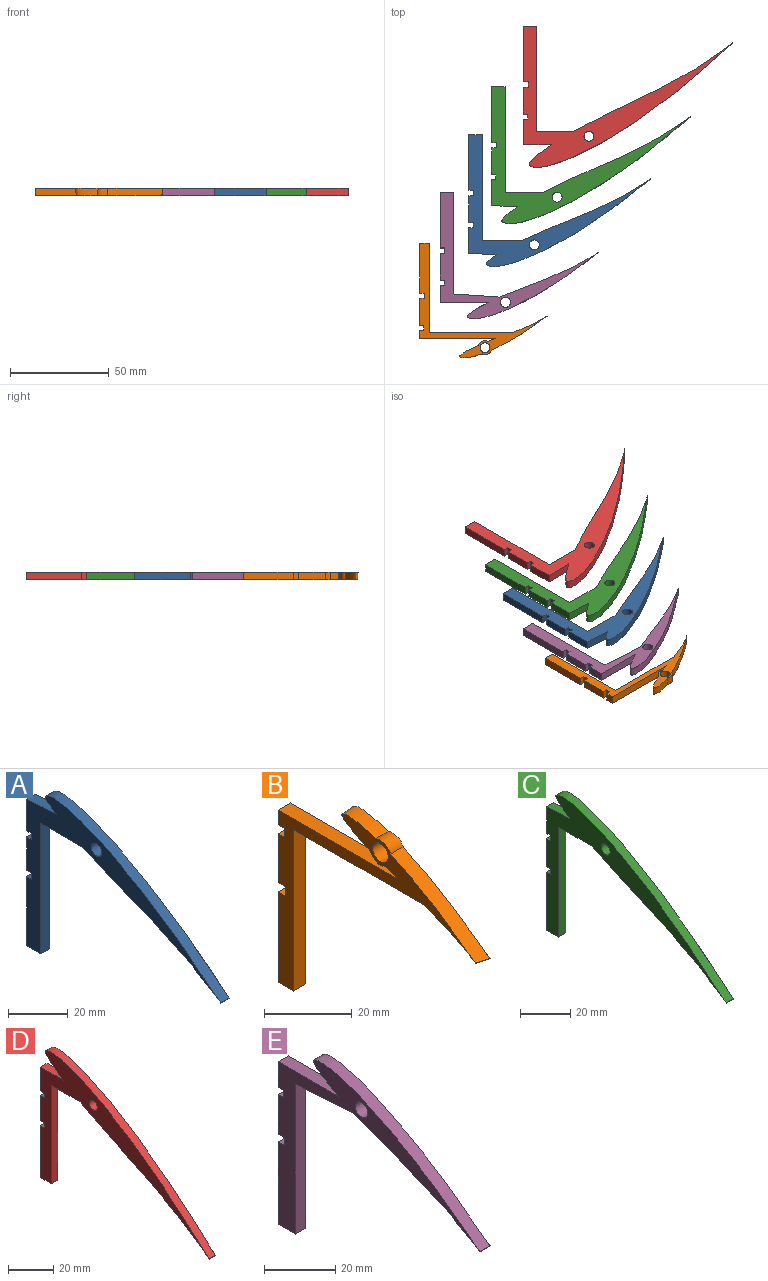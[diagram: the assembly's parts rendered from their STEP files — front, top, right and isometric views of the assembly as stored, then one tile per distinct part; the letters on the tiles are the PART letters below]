
ASSEMBLY  parts=5 mates=4
PART A: 19 faces, bbox 4x92x66.8 mm
  f0: plane 13.63x4mm, normal (0,1,0), area 54.5mm2, adj f2,f3,f13,f17
  f1: plane 28.27x4mm, normal (0,1,0), area 113.1mm2, adj f2,f3,f9,f12
  f2: plane 91.96x66.78mm, normal (-1,0,0), area 1042.6mm2, adj f0,f1,f4,f5,f6,f7,f8,f9
  f3: plane 91.96x66.78mm, normal (1,0,0), area 1042.6mm2, adj f0,f1,f4,f5,f6,f7,f8,f9
  f4: extruded ~81.29x43.68mm, area 702.9mm2, adj f2,f3,f5,f6
  f5: plane 4x0.96mm, normal (0,0,1), area 3.8mm2, adj f2,f3,f4,f7
  f6: plane 4x1.11mm, normal (0,-0.15,-0.99), area 4.5mm2, adj f2,f3,f4,f11
  f7: plane 13.06x4mm, normal (0,0.05,1), area 52.3mm2, adj f2,f3,f5,f8
  f8: plane 12.99x4mm, normal (0,1,0), area 51.9mm2, adj f2,f3,f7,f15
  f9: plane 6.75x4mm, normal (0,0,-1), area 27mm2, adj f1,f2,f3,f10
  f10: plane 53.49x4mm, normal (0,-1,0), area 214mm2, adj f2,f3,f9,f11
  f11: plane 18.8x4mm, normal (0,0,-1), area 75.2mm2, adj f2,f3,f6,f10
  f12: plane 4x2.41mm, normal (0,0,1), area 9.6mm2, adj f1,f2,f3,f14
  f13: plane 4x2.41mm, normal (0,0,-1), area 9.6mm2, adj f0,f2,f3,f14
  f14: plane 4x2.64mm, normal (0,1,0), area 10.5mm2, adj f2,f3,f12,f13
  f15: plane 4x2.18mm, normal (0,0,-1), area 8.7mm2, adj f2,f3,f8,f16
  f16: plane 4x2.52mm, normal (0,1,0), area 10.1mm2, adj f2,f3,f15,f17
  f17: plane 4x2.18mm, normal (0,0,1), area 8.7mm2, adj f0,f2,f3,f16
  f18: cylinder r=2.5mm len=5mm, axis (1,0,0), area 62.8mm2, adj f2,f3
PART B: 21 faces, bbox 61.1x65x59.3 mm
  f0: plane 13.63x4mm, normal (0,1,0), area 54.5mm2, adj f2,f3,f15,f19
  f1: plane 25.19x4mm, normal (0,1,0), area 100.8mm2, adj f2,f3,f13,f14
  f2: plane 65.03x58.52mm, normal (1,0,0), area 472.4mm2, adj f0,f1,f4,f5,f6,f7,f8,f9
  f3: plane 64.35x58.3mm, normal (-1,0,0), area 470.3mm2, adj f0,f1,f4,f5,f6,f7,f8,f9
  f4: bspline ~28.12x17.14mm, area 207.3mm2, adj f2,f3,f5,f10
  f5: cylinder r=3.5mm len=4.86mm, axis (-1,0,0), area 23.4mm2, adj f2,f3,f4,f8
  f6: cylinder r=3.5mm len=4.83mm, axis (-1,0,0), area 23.2mm2, adj f2,f3,f7,f8
  f7: bspline ~60.49x6.24mm, area 17.6mm2, adj f2,f3,f6,f11
  f8: bspline ~60.49x13.41mm, area 90.8mm2, adj f2,f3,f5,f6
  f9: plane 45.11x4mm, normal (0,-1,0), area 180.4mm2, adj f2,f3,f10,f13
  f10: plane 42.24x4.01mm, normal (0,0,-1), area 168.5mm2, adj f2,f3,f4,f9
  f11: plane 38.84x4.01mm, normal (0,0,1), area 155mm2, adj f2,f3,f7,f12
  f12: plane 4.08x4mm, normal (0,1,0), area 16.3mm2, adj f2,f3,f11,f17
  f13: plane 5.04x4mm, normal (0,0,-1), area 20.1mm2, adj f1,f2,f3,f9
  f14: plane 4x2.41mm, normal (0,0,1), area 9.6mm2, adj f1,f2,f3,f16
  f15: plane 4x2.41mm, normal (0,0,-1), area 9.6mm2, adj f0,f2,f3,f16
  f16: plane 4x2.64mm, normal (0,1,0), area 10.5mm2, adj f2,f3,f14,f15
  f17: plane 4x2.18mm, normal (0,0,-1), area 8.7mm2, adj f2,f3,f12,f18
  f18: plane 4x2.52mm, normal (0,1,0), area 10.1mm2, adj f2,f3,f17,f19
  f19: plane 4x2.18mm, normal (0,0,1), area 8.7mm2, adj f0,f2,f3,f18
  f20: cylinder r=2.5mm len=5mm, axis (1,0,0), area 62.8mm2, adj f2,f3
PART C: 17 faces, bbox 4x100.8x69.3 mm
  f0: plane 13.63x4mm, normal (0,1,0), area 54.5mm2, adj f2,f3,f11,f15
  f1: plane 28.27x4mm, normal (0,1,0), area 113.1mm2, adj f2,f3,f8,f10
  f2: plane 100.76x69.26mm, normal (-1,0,0), area 1079.5mm2, adj f0,f1,f4,f5,f6,f7,f8,f9
  f3: plane 100.76x69.26mm, normal (1,0,0), area 1079.5mm2, adj f0,f1,f4,f5,f6,f7,f8,f9
  f4: extruded ~93.53x53.84mm, area 829.8mm2, adj f2,f3,f5,f6
  f5: plane 18.8x4mm, normal (0,0,-1), area 75.2mm2, adj f2,f3,f4,f9
  f6: plane 13.06x4mm, normal (0,0.05,1), area 52.3mm2, adj f2,f3,f4,f7
  f7: plane 12.99x4mm, normal (0,1,0), area 51.9mm2, adj f2,f3,f6,f13
  f8: plane 6.75x4mm, normal (0,0,-1), area 27mm2, adj f1,f2,f3,f9
  f9: plane 53.49x4mm, normal (0,-1,0), area 214mm2, adj f2,f3,f5,f8
  f10: plane 4x2.41mm, normal (0,0,1), area 9.6mm2, adj f1,f2,f3,f12
  f11: plane 4x2.41mm, normal (0,0,-1), area 9.6mm2, adj f0,f2,f3,f12
  f12: plane 4x2.64mm, normal (0,1,0), area 10.5mm2, adj f2,f3,f10,f11
  f13: plane 4x2.18mm, normal (0,0,-1), area 8.7mm2, adj f2,f3,f7,f14
  f14: plane 4x2.52mm, normal (0,1,0), area 10.1mm2, adj f2,f3,f13,f15
  f15: plane 4x2.18mm, normal (0,0,1), area 8.7mm2, adj f0,f2,f3,f14
  f16: cylinder r=2.5mm len=5mm, axis (1,0,0), area 62.8mm2, adj f2,f3
PART D: 18 faces, bbox 4x105.7x71.5 mm
  f0: plane 13.63x4mm, normal (0,1,0), area 54.5mm2, adj f2,f3,f12,f16
  f1: plane 28.27x4mm, normal (0,1,0), area 113.1mm2, adj f2,f3,f8,f11
  f2: plane 105.66x71.45mm, normal (-1,0,0), area 1024.1mm2, adj f0,f1,f4,f6,f7,f8,f9,f10
  f3: plane 105.66x71.45mm, normal (1,0,0), area 1023.1mm2, adj f0,f1,f4,f6,f7,f8,f9,f10
  f4: extruded ~101.67x62.04mm, area 923.7mm2, adj f2,f3,f5,f6
  f5: plane 4.01x0.01mm, normal (0,-0.64,0.77), area 0mm2, adj f4,f10
  f6: plane 14.14x4mm, normal (0,0,1), area 56.6mm2, adj f2,f3,f4,f7
  f7: plane 12.99x4mm, normal (0,1,0), area 51.9mm2, adj f2,f3,f6,f14
  f8: plane 6.75x4mm, normal (0,0,-1), area 27mm2, adj f1,f2,f3,f9
  f9: plane 53.49x4mm, normal (0,-1,0), area 214mm2, adj f2,f3,f8,f10
  f10: plane 18.12x4mm, normal (0,0,-1), area 72.5mm2, adj f2,f3,f5,f9
  f11: plane 4x2.41mm, normal (0,0,1), area 9.6mm2, adj f1,f2,f3,f13
  f12: plane 4x2.41mm, normal (0,0,-1), area 9.6mm2, adj f0,f2,f3,f13
  f13: plane 4x2.64mm, normal (0,1,0), area 10.5mm2, adj f2,f3,f11,f12
  f14: plane 4x2.18mm, normal (0,0,-1), area 8.7mm2, adj f2,f3,f7,f15
  f15: plane 4x2.52mm, normal (0,1,0), area 10.1mm2, adj f2,f3,f14,f16
  f16: plane 4x2.18mm, normal (0,0,1), area 8.7mm2, adj f0,f2,f3,f15
  f17: cylinder r=2.5mm len=5mm, axis (1,0,0), area 62.8mm2, adj f2,f3
PART E: 17 faces, bbox 4x80x64.1 mm
  f0: plane 13.63x4mm, normal (0,1,0), area 54.5mm2, adj f2,f3,f11,f15
  f1: plane 28.27x4mm, normal (0,1,0), area 113.1mm2, adj f2,f3,f8,f10
  f2: plane 80.02x64.08mm, normal (-1,0,0), area 692.2mm2, adj f0,f1,f4,f5,f6,f7,f8,f9
  f3: plane 80.02x64.08mm, normal (1,0,0), area 692.2mm2, adj f0,f1,f4,f5,f6,f7,f8,f9
  f4: extruded ~64.88x32.79mm, area 572.7mm2, adj f2,f3,f5,f6
  f5: plane 23.36x4mm, normal (0,-0.07,-1), area 93.7mm2, adj f2,f3,f4,f9
  f6: plane 24.35x4mm, normal (0,0,1), area 97.4mm2, adj f2,f3,f4,f7
  f7: plane 8.73x4mm, normal (0,1,0), area 34.9mm2, adj f2,f3,f6,f13
  f8: plane 6.75x4mm, normal (0,0,-1), area 27mm2, adj f1,f2,f3,f9
  f9: plane 51.51x4mm, normal (0,-1,0), area 206.1mm2, adj f2,f3,f5,f8
  f10: plane 4x2.41mm, normal (0,0,1), area 9.6mm2, adj f1,f2,f3,f12
  f11: plane 4x2.41mm, normal (0,0,-1), area 9.6mm2, adj f0,f2,f3,f12
  f12: plane 4x2.64mm, normal (0,1,0), area 10.5mm2, adj f2,f3,f10,f11
  f13: plane 4x2.18mm, normal (0,0,-1), area 8.7mm2, adj f2,f3,f7,f14
  f14: plane 4x2.52mm, normal (0,1,0), area 10.1mm2, adj f2,f3,f13,f15
  f15: plane 4x2.18mm, normal (0,0,1), area 8.7mm2, adj f0,f2,f3,f14
  f16: cylinder r=2.5mm len=5mm, axis (1,0,0), area 62.8mm2, adj f2,f3
PLACE A rot(axis=(0.58,-0.58,0.58),120deg) t=(-215.66,-141.68,1603.14)mm
PLACE B rot(axis=(0.58,-0.58,0.58),120deg) t=(-240.57,-193.64,1807.14)mm
PLACE C rot(axis=(0.58,-0.58,0.58),120deg) t=(-204.11,-117.52,1501.14)mm
PLACE D rot(axis=(0.58,-0.58,0.58),120deg) t=(-188.02,-86.79,1399.14)mm
PLACE E rot(axis=(0.58,-0.58,0.58),120deg) t=(-230.23,-170.76,1705.14)mm
MATE planar E.f3 <-> A.f3  axis (0,0,1) through (-243.44,-155.3,181.14)mm
MATE planar B.f5 <-> E.f3  axis (0,0,1) through (-240.57,-193.64,181.14)mm
MATE planar A.f3 <-> C.f3  axis (0,0,1) through (-224.73,-129.18,181.14)mm
MATE planar C.f3 <-> D.f3  axis (0,0,1) through (-211.65,-115.23,181.14)mm
